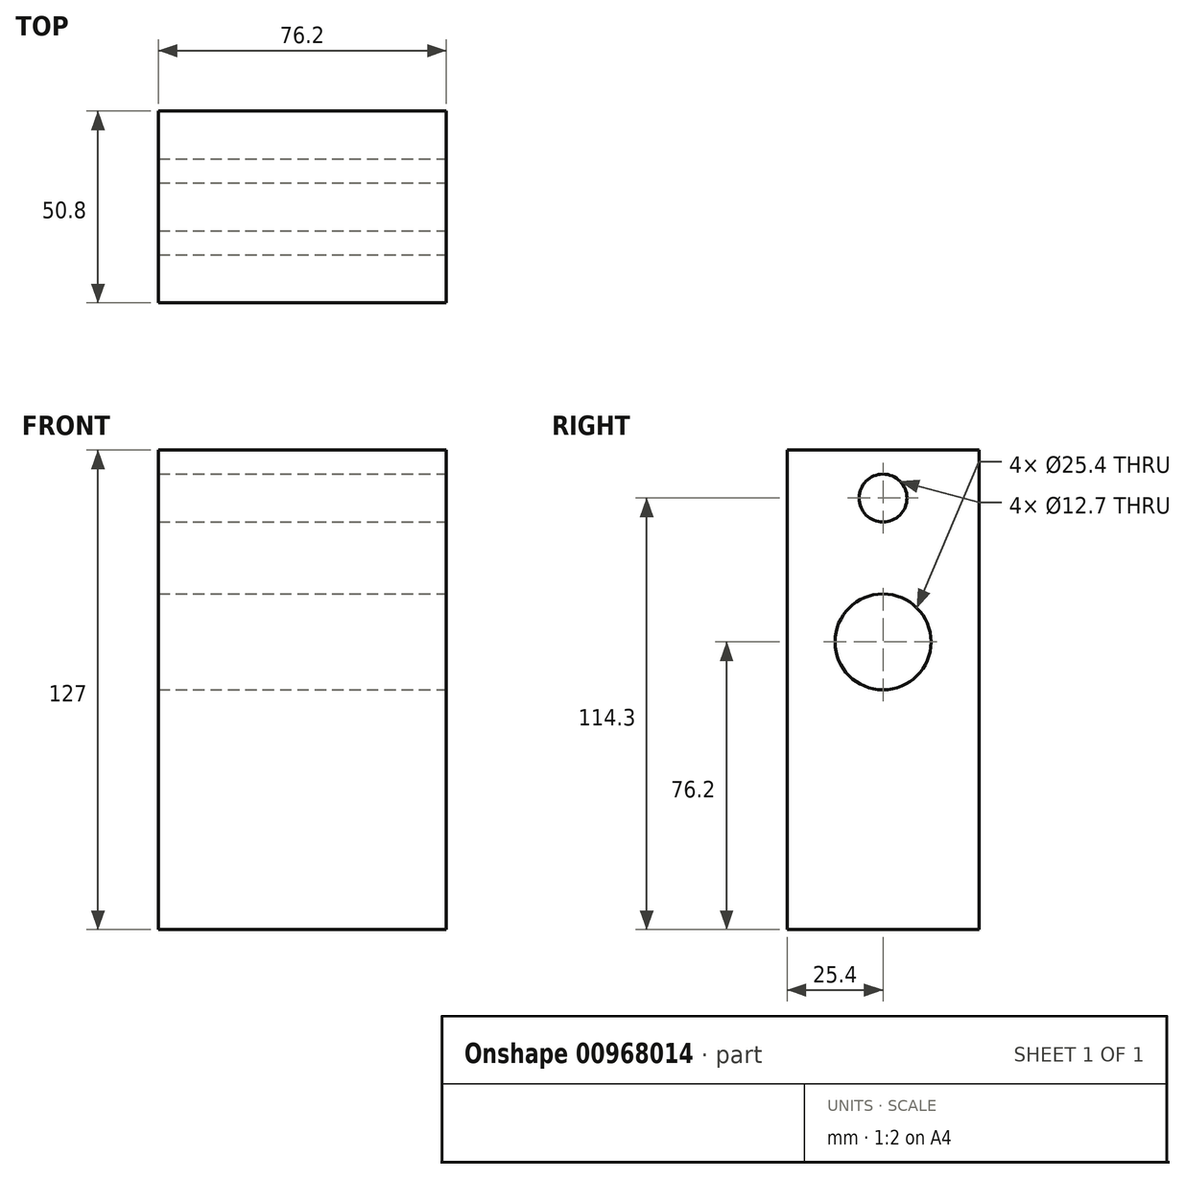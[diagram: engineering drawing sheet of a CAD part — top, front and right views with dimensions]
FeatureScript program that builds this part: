
annotation { "Feature Type Name" : "Feature", "Feature Type Description" : "" }
export const myFeature = defineFeature(function(context is Context, id is Id, definition is map)
    precondition{}
    {
        {
            var Q0;
            Q0=qCreatedBy(makeId("Top.planeOp"),FACE);
            var sketch = newSketch(context, id + "F0", { "sketchPlane" : qUnion([Q0])});
            skLineSegment(sketch, "E0.bottom", {"start": v(-38.1, 25.4) * mm, "end": v(38.1, 25.4) * mm});
            skLineSegment(sketch, "E0.top", {"start": v(-38.1, -25.4) * mm, "end": v(38.1, -25.4) * mm});
            skLineSegment(sketch, "E0.left", {"start": v(-38.1, 25.4) * mm, "end": v(-38.1, -25.4) * mm});
            skLineSegment(sketch, "E0.right", {"start": v(38.1, 25.4) * mm, "end": v(38.1, -25.4) * mm});
            skSolve(sketch);
        }
        {
            var Q0;
            Q0 = qSketchRegion(id + "F0", true);
            extrude(context, id + "F1", {"entities" : qUnion([Q0]), "depth" : 127 * mm, "offsetDistance" : 25.4 * mm});
        }
        {
            var Q0;
            Q0=makeQuery(id+"F1.opExtrude","SWEPT_FACE",FACE,{"disambiguationData":[OSD([sQuery(id+"F0.wireOp",EDGE,"E0.right")])]});
            var sketch = newSketch(context, id + "F2", { "sketchPlane" : qUnion([Q0])});
            skCircle(sketch, "E1", {"center": v(0, 76.2) * mm, "radius": 12.7 * mm});
            skSolve(sketch);
        }
        {
            var Q0;
            Q0=sQuery(id+"F2.wireOp",VERTEX,"E1.center");
            var Q1;
            Q1=makeQuery(id+"F1.opExtrude","SWEPT_BODY",BODY,{"disambiguationData":[OSD([sQuery(id+"F0.wireOp",EDGE,"E0.bottom"),sQuery(id+"F0.wireOp",EDGE,"E0.top"),sQuery(id+"F0.wireOp",EDGE,"E0.left"),sQuery(id+"F0.wireOp",EDGE,"E0.right")])]});
            hole(context, id + "F3", {"style" : HoleStyle.SIMPLE, "endStyle" : HoleEndStyle.THROUGH, "holeDiameter" : 25.4 * mm, "majorDiameter" : 6.35 * mm, "isTappedThrough" : true, "tappedDepth" : 12.7 * mm, "tapClearance" : 3, "locations" : qUnion([Q0]), "scope" : qUnion([Q1])});
        }
        {
            var Q0;
            Q0=makeQuery(id+"F1.opExtrude","SWEPT_FACE",FACE,{"disambiguationData":[OSD([sQuery(id+"F0.wireOp",EDGE,"E0.right")])]});
            var sketch = newSketch(context, id + "F4", { "sketchPlane" : qUnion([Q0])});
            skCircle(sketch, "E2", {"center": v(0, 114.3) * mm, "radius": 6.35 * mm});
            skSolve(sketch);
        }
        {
            var Q0;
            Q0=sQuery(id+"F4.wireOp",VERTEX,"E2.center");
            var Q1;
            Q1=makeQuery(id+"F1.opExtrude","SWEPT_BODY",BODY,{"disambiguationData":[OSD([sQuery(id+"F0.wireOp",EDGE,"E0.bottom"),sQuery(id+"F0.wireOp",EDGE,"E0.top"),sQuery(id+"F0.wireOp",EDGE,"E0.left"),sQuery(id+"F0.wireOp",EDGE,"E0.right")])]});
            hole(context, id + "F5", {"style" : HoleStyle.SIMPLE, "endStyle" : HoleEndStyle.THROUGH, "holeDiameter" : 12.7 * mm, "majorDiameter" : 6.35 * mm, "isTappedThrough" : true, "tappedDepth" : 12.7 * mm, "tapClearance" : 3, "locations" : qUnion([Q0]), "scope" : qUnion([Q1])});
        }
    });
